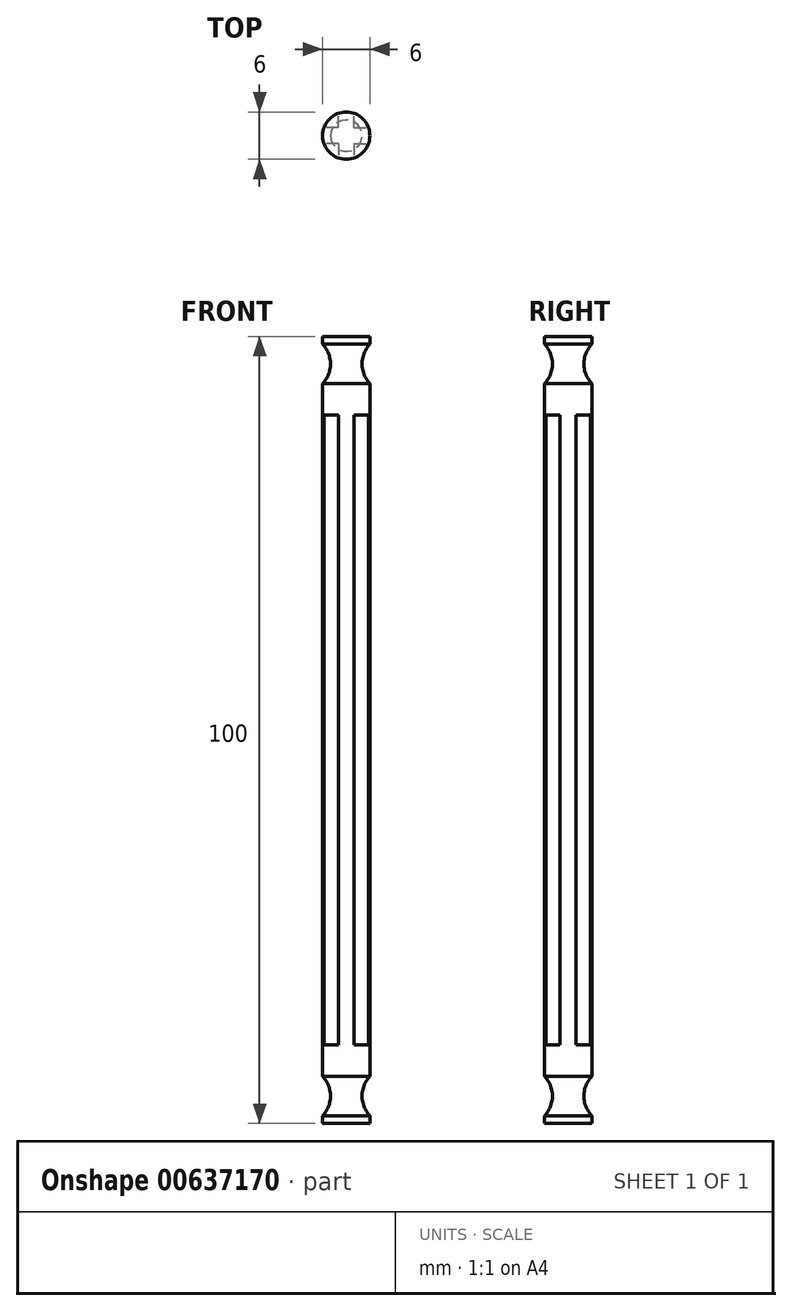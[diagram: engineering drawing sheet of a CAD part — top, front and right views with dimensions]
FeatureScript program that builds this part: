
annotation { "Feature Type Name" : "Feature", "Feature Type Description" : "" }
export const myFeature = defineFeature(function(context is Context, id is Id, definition is map)
    precondition{}
    {
        {
            var Q0;
            Q0=qCreatedBy(makeId("Front.planeOp"),FACE);
            var sketch = newSketch(context, id + "F0", { "sketchPlane" : qUnion([Q0])});
            skLineSegment(sketch, "E0", {"start": v(0, -50) * mm, "end": v(3, -50) * mm});
            skLineSegment(sketch, "E1", {"start": v(3, -50) * mm, "end": v(3, 0) * mm});
            skArc(sketch, "E2", {"start": v(3, -44) * mm, "mid": v(2, -46.5) * mm, "end": v(3, -49) * mm});
            skLineSegment(sketch, "E3", {"start": v(0, -50) * mm, "end": v(0, 50) * mm});
            skLineSegment(sketch, "E4.MirrorCS", {"start": v(0, 50) * mm, "end": v(3, 50) * mm});
            skArc(sketch, "E5.MirrorCS", {"start": v(3, 44) * mm, "mid": v(2, 46.5) * mm, "end": v(3, 49) * mm});
            skLineSegment(sketch, "E6.MirrorCS", {"start": v(3, 50) * mm, "end": v(3, 0) * mm});
            skPoint(sketch, "E7", {"position": v(0, -40) * mm});
            skPoint(sketch, "E8.MirrorP", {"position": v(0, 40) * mm});
            skSolve(sketch);
        }
        {
            var Q0;
            {var subQ3=sQuery(id+"F0.wireOp",EDGE,"E0");Q0=makeQuery(id+"F0.imprint","IMPRINT",FACE,{"disambiguationData":[TD([[makeQuery(id+"F0.imprint","IMPRINT",EDGE,{"derivedFrom":subQ3}),1.0]])]});}
            var Q1;
            {var subQ1=sQuery(id+"F0.wireOp",EDGE,"kCGa6llR-Nuby-u7u0-b5NF-3Ijth7emAabv");Q1=makeQuery(id+"F0.imprint","IMPRINT",FACE,{"disambiguationData":[TD([[makeQuery(id+"F0.imprint","IMPRINT",EDGE,{"derivedFrom":subQ1}),1.0]])]});}
            var Q2;
            Q2=sQuery(id+"F0.wireOp",EDGE,"E3");
            revolve(context, id + "F1", {"entities" : qUnion([Q0, Q1]), "axis" : qUnion([Q2]), "revolveType" : RevolveType.FULL});
        }
        {
            var Q0;
            Q0=qCreatedBy(makeId("Top.planeOp"),FACE);
            var sketch = newSketch(context, id + "F2", { "sketchPlane" : qUnion([Q0])});
            skLineSegment(sketch, "E9.bottom", {"start": v(1, 1) * mm, "end": v(3, 1) * mm});
            skLineSegment(sketch, "E9.top", {"start": v(1, 3) * mm, "end": v(3, 3) * mm});
            skLineSegment(sketch, "E9.left", {"start": v(1, 1) * mm, "end": v(1, 3) * mm});
            skLineSegment(sketch, "E9.right", {"start": v(3, 1) * mm, "end": v(3, 3) * mm});
            skLineSegment(sketch, "E10.1.0", {"start": v(-1, 1) * mm, "end": v(-3, 1) * mm});
            skLineSegment(sketch, "E10.1.1", {"start": v(-3, 1) * mm, "end": v(-3, 3) * mm});
            skLineSegment(sketch, "E10.1.2", {"start": v(-1, 3) * mm, "end": v(-3, 3) * mm});
            skLineSegment(sketch, "E10.1.3", {"start": v(-1, 1) * mm, "end": v(-1, 3) * mm});
            skLineSegment(sketch, "E10.2.0", {"start": v(-1, -1) * mm, "end": v(-1, -3) * mm});
            skLineSegment(sketch, "E10.2.1", {"start": v(-1, -3) * mm, "end": v(-3, -3) * mm});
            skLineSegment(sketch, "E10.2.2", {"start": v(-3, -1) * mm, "end": v(-3, -3) * mm});
            skLineSegment(sketch, "E10.2.3", {"start": v(-1, -1) * mm, "end": v(-3, -1) * mm});
            skLineSegment(sketch, "E10.3.0", {"start": v(1, -1) * mm, "end": v(3, -1) * mm});
            skLineSegment(sketch, "E10.3.1", {"start": v(3, -1) * mm, "end": v(3, -3) * mm});
            skLineSegment(sketch, "E10.3.2", {"start": v(1, -3) * mm, "end": v(3, -3) * mm});
            skLineSegment(sketch, "E10.3.3", {"start": v(1, -1) * mm, "end": v(1, -3) * mm});
            skPoint(sketch, "E10.center", {"position": v(0, 0) * mm});
            skLineSegment(sketch, "E11", {"start": v(-1, 1) * mm, "end": v(1, 1) * mm});
            skSolve(sketch);
        }
        {
            var Q0;
            Q0 = qSketchRegion(id + "F2", true);
            var Q1;
            Q1=sQuery(id+"F0.wireOp",VERTEX,"E7");
            var Q2;
            Q2=sQuery(id+"F0.wireOp",VERTEX,"E8.MirrorP");
            extrude(context, id + "F3", {"entities" : qUnion([Q0]), "operationType" : NewBodyOperationType.REMOVE, "endBound" : BoundingType.UP_TO_VERTEX, "oppositeDirection" : true, "depth" : 25 * mm, "endBoundEntityVertex" : qUnion([Q1]), "offsetDistance" : 25 * mm, "hasSecondDirection" : true, "secondDirectionBound" : SecondDirectionBoundingType.UP_TO_VERTEX, "secondDirectionOppositeDirection" : false, "secondDirectionDepth" : 25 * mm, "secondDirectionBoundEntityVertex" : qUnion([Q2])});
        }
    });
